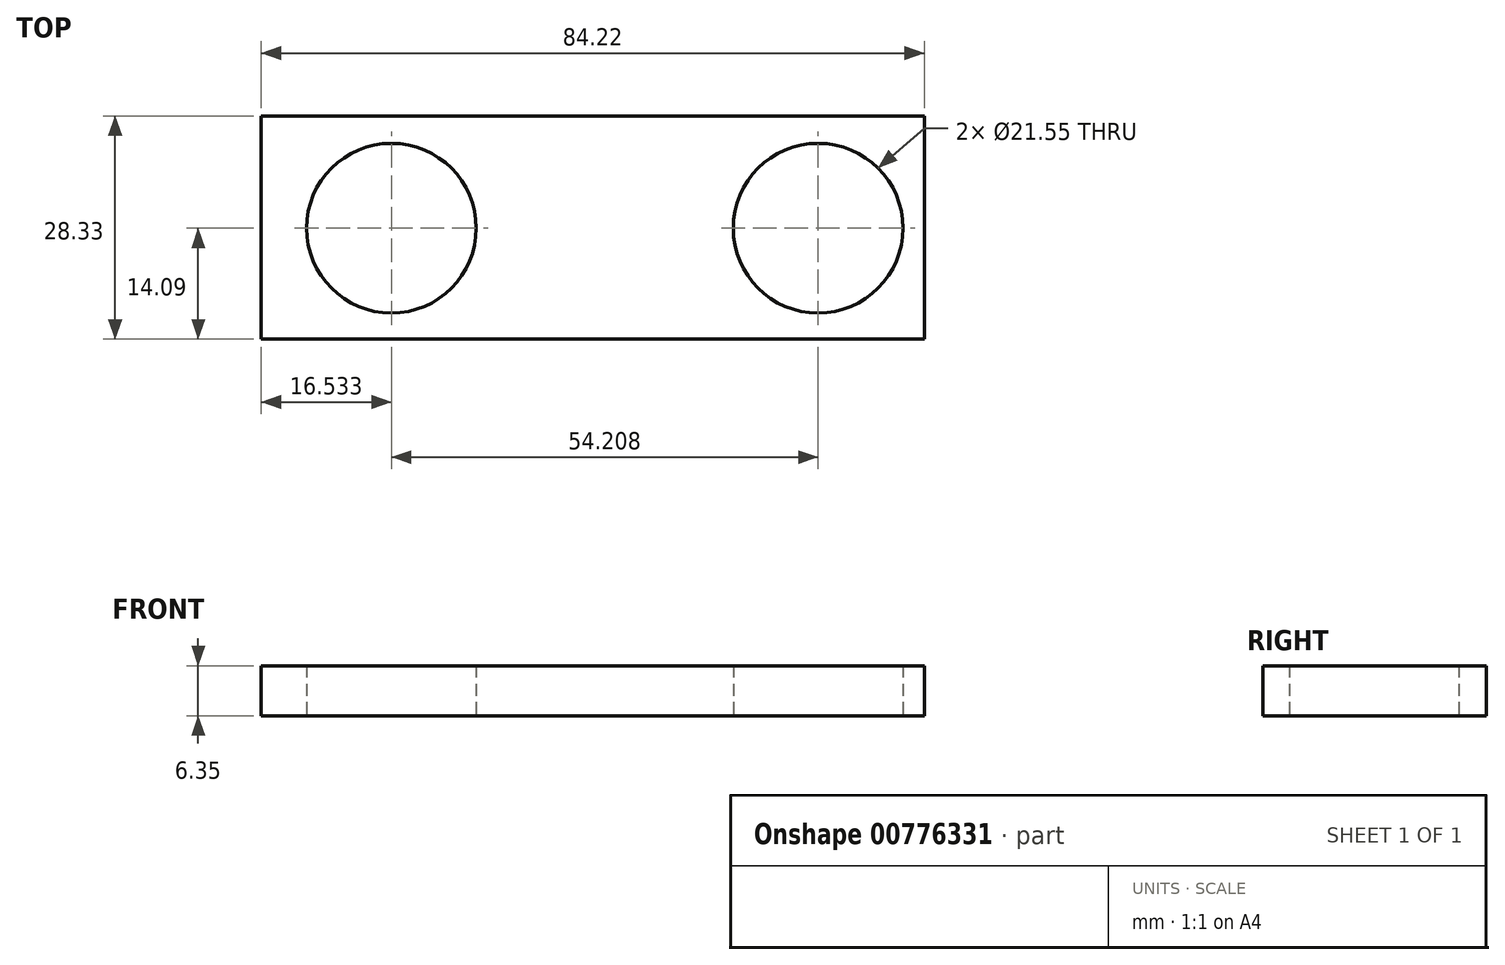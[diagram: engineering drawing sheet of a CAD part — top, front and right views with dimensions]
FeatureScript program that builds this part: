
annotation { "Feature Type Name" : "Feature", "Feature Type Description" : "" }
export const myFeature = defineFeature(function(context is Context, id is Id, definition is map)
    precondition{}
    {
        {
            var Q0;
            Q0=qCreatedBy(makeId("Top.planeOp"),FACE);
            var sketch = newSketch(context, id + "F0", { "sketchPlane" : qUnion([Q0])});
            skCircle(sketch, "E0", {"center": v(-47.55, 0) * mm, "radius": 10.78 * mm});
            skCircle(sketch, "E1", {"center": v(6.66, 0) * mm, "radius": 10.78 * mm});
            skLineSegment(sketch, "E2.bottom", {"start": v(-64.08, 14.24) * mm, "end": v(20.14, 14.24) * mm});
            skLineSegment(sketch, "E2.top", {"start": v(-64.08, -14.09) * mm, "end": v(20.14, -14.09) * mm});
            skLineSegment(sketch, "E2.left", {"start": v(-64.08, 14.24) * mm, "end": v(-64.08, -14.09) * mm});
            skLineSegment(sketch, "E2.right", {"start": v(20.14, 14.24) * mm, "end": v(20.14, -14.09) * mm});
            skSolve(sketch);
        }
        {
            var Q0;
            Q0=makeQuery(id+"F0.imprint","IMPRINT",FACE,{"disambiguationData":[TD([[makeQuery(id+"F0.imprint","IMPRINT",EDGE,{"derivedFrom":sQuery(id+"F0.wireOp",EDGE,"E0")}),-1.0]])]});
            extrude(context, id + "F1", {"entities" : qUnion([Q0]), "depth" : 6.35 * mm, "offsetDistance" : 25.4 * mm});
        }
    });
